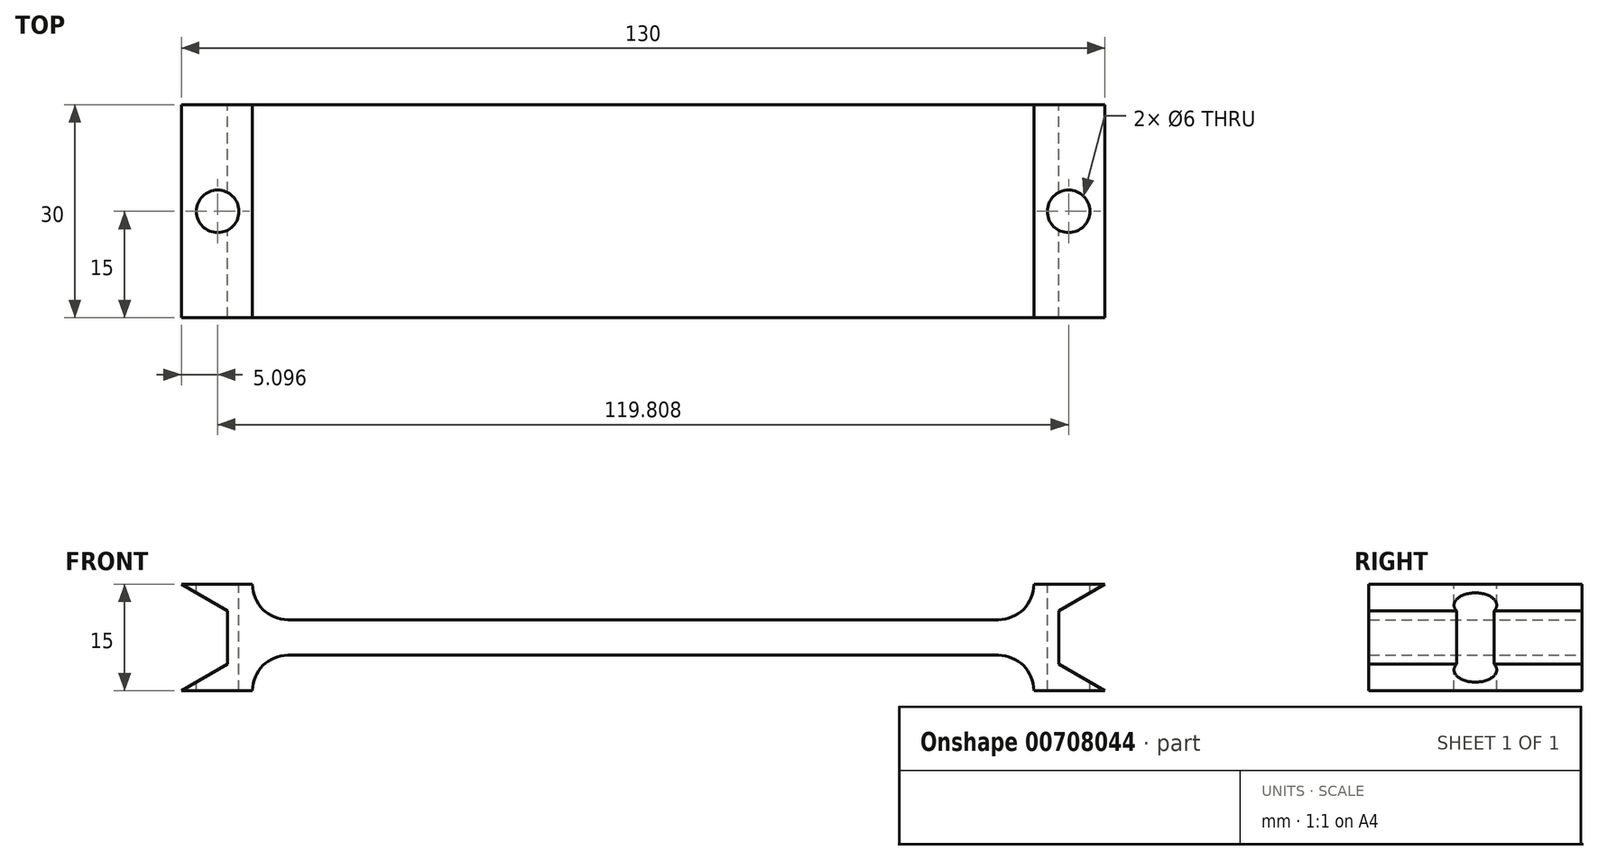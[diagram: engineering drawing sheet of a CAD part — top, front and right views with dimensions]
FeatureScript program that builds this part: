
annotation { "Feature Type Name" : "Feature", "Feature Type Description" : "" }
export const myFeature = defineFeature(function(context is Context, id is Id, definition is map)
    precondition{}
    {
        {
            var Q0;
            Q0=qCreatedBy(makeId("Front.planeOp"),FACE);
            var sketch = newSketch(context, id + "F0", { "sketchPlane" : qUnion([Q0])});
            skLineSegment(sketch, "E0.bottom", {"start": v(-15, -7.5) * mm, "end": v(15, -7.5) * mm});
            skLineSegment(sketch, "E0.top", {"start": v(-15, 7.5) * mm, "end": v(15, 7.5) * mm});
            skLineSegment(sketch, "E0.left", {"start": v(-15, -7.5) * mm, "end": v(-15, 7.5) * mm});
            skLineSegment(sketch, "E0.right", {"start": v(15, -7.5) * mm, "end": v(15, 7.5) * mm});
            skPoint(sketch, "E0.middle", {"position": v(0, 0) * mm});
            skCircle(sketch, "E1", {"center": v(-15, 7.5) * mm, "radius": 5 * mm});
            skCircle(sketch, "E2", {"center": v(15, 7.5) * mm, "radius": 5 * mm});
            skCircle(sketch, "E3", {"center": v(-15, -7.5) * mm, "radius": 5 * mm});
            skCircle(sketch, "E4", {"center": v(15, -7.5) * mm, "radius": 5 * mm});
            skCircle(sketch, "E5.cCircle", {"center": v(0, 0) * mm, "radius": 7.5 * mm, "construction": true});
            skLineSegment(sketch, "E5.0", {"start": v(0, -7.5) * mm, "end": v(-6.5, -3.75) * mm});
            skLineSegment(sketch, "E5.1", {"start": v(-6.5, -3.75) * mm, "end": v(-6.5, 3.75) * mm});
            skLineSegment(sketch, "E5.2", {"start": v(-6.5, 3.75) * mm, "end": v(0, 7.5) * mm});
            skLineSegment(sketch, "E5.3", {"start": v(0, 7.5) * mm, "end": v(6.5, 3.75) * mm});
            skLineSegment(sketch, "E5.4", {"start": v(6.5, 3.75) * mm, "end": v(6.5, -3.75) * mm});
            skLineSegment(sketch, "E5.5", {"start": v(6.5, -3.75) * mm, "end": v(0, -7.5) * mm});
            skSolve(sketch);
        }
        {
            var Q0;
            {var subQ8=sQuery(id+"F0.wireOp",EDGE,"E5.0");Q0=makeQuery(id+"F0.imprint","IMPRINT",FACE,{"disambiguationData":[TD([[makeQuery(id+"F0.imprint","IMPRINT",EDGE,{"derivedFrom":subQ8}),1.0]])]});}
            extrude(context, id + "F1", {"entities" : qUnion([Q0]), "depth" : 30 * mm, "offsetDistance" : 25 * mm});
        }
        {
            var Q0;
            Q0=makeQuery(id+"F1.opExtrude","SWEPT_FACE",FACE,{"disambiguationData":[OSD([sQuery(id+"F0.wireOp",EDGE,"E0.top")])]});
            var sketch = newSketch(context, id + "F2", { "sketchPlane" : qUnion([Q0])});
            skCircle(sketch, "E6", {"center": v(-5.1, -15) * mm, "radius": 3 * mm});
            skPoint(sketch, "E6.centerSnap0", {"position": v(0, -15) * mm});
            skSolve(sketch);
        }
        {
            var Q0;
            Q0=makeQuery(id+"F2.imprint","IMPRINT",FACE,{"disambiguationData":[TD([[makeQuery(id+"F2.imprint","IMPRINT",EDGE,{"derivedFrom":sQuery(id+"F2.wireOp",EDGE,"E6")}),1.0]])]});
            var Q1;
            Q1=sQuery(id+"F2.wireOp",EDGE,"E6");
            var Q2;
            Q2=makeQuery(id+"F1.opExtrude","SWEPT_FACE",FACE,{"disambiguationData":[OSD([sQuery(id+"F0.wireOp",EDGE,"E0.bottom")])]});
            extrude(context, id + "F3", {"entities" : qUnion([Q0]), "operationType" : NewBodyOperationType.REMOVE, "surfaceEntities" : qUnion([Q1]), "endBound" : BoundingType.UP_TO_SURFACE, "oppositeDirection" : true, "depth" : 25 * mm, "endBoundEntityFace" : qUnion([Q2]), "offsetDistance" : 25 * mm});
        }
        {
            var Q0;
            Q0=makeQuery(id+"F1.opExtrude","SWEPT_FACE",FACE,{"disambiguationData":[OSD([sQuery(id+"F0.wireOp",EDGE,"E0.left")])]});
            extrude(context, id + "F4", {"entities" : qUnion([Q0]), "operationType" : NewBodyOperationType.ADD, "depth" : 50 * mm, "offsetDistance" : 25 * mm});
        }
        {
            var Q0;
            Q0=makeQuery(id+"F1.opExtrude","SWEPT_BODY",BODY,{"disambiguationData":[OSD([sQuery(id+"F0.wireOp",EDGE,"E0.bottom"),sQuery(id+"F0.wireOp",EDGE,"E0.top"),sQuery(id+"F0.wireOp",EDGE,"E0.left"),sQuery(id+"F0.wireOp",EDGE,"E1"),sQuery(id+"F0.wireOp",EDGE,"E3"),sQuery(id+"F0.wireOp",EDGE,"E5.0"),sQuery(id+"F0.wireOp",EDGE,"E5.1"),sQuery(id+"F0.wireOp",EDGE,"E5.2")])]});
            var Q1;
            Q1=makeQuery(id+"F4.opExtrude","CAP_FACE",FACE,{"disambiguationData":[OSD([sQuery(id+"F0.wireOp",EDGE,"E0.left")])],"isStart":false});
            mirror(context, id + "F5", {"operationType" : NewBodyOperationType.ADD, "entities" : qUnion([Q0]), "mirrorPlane" : qUnion([Q1])});
        }
    });
